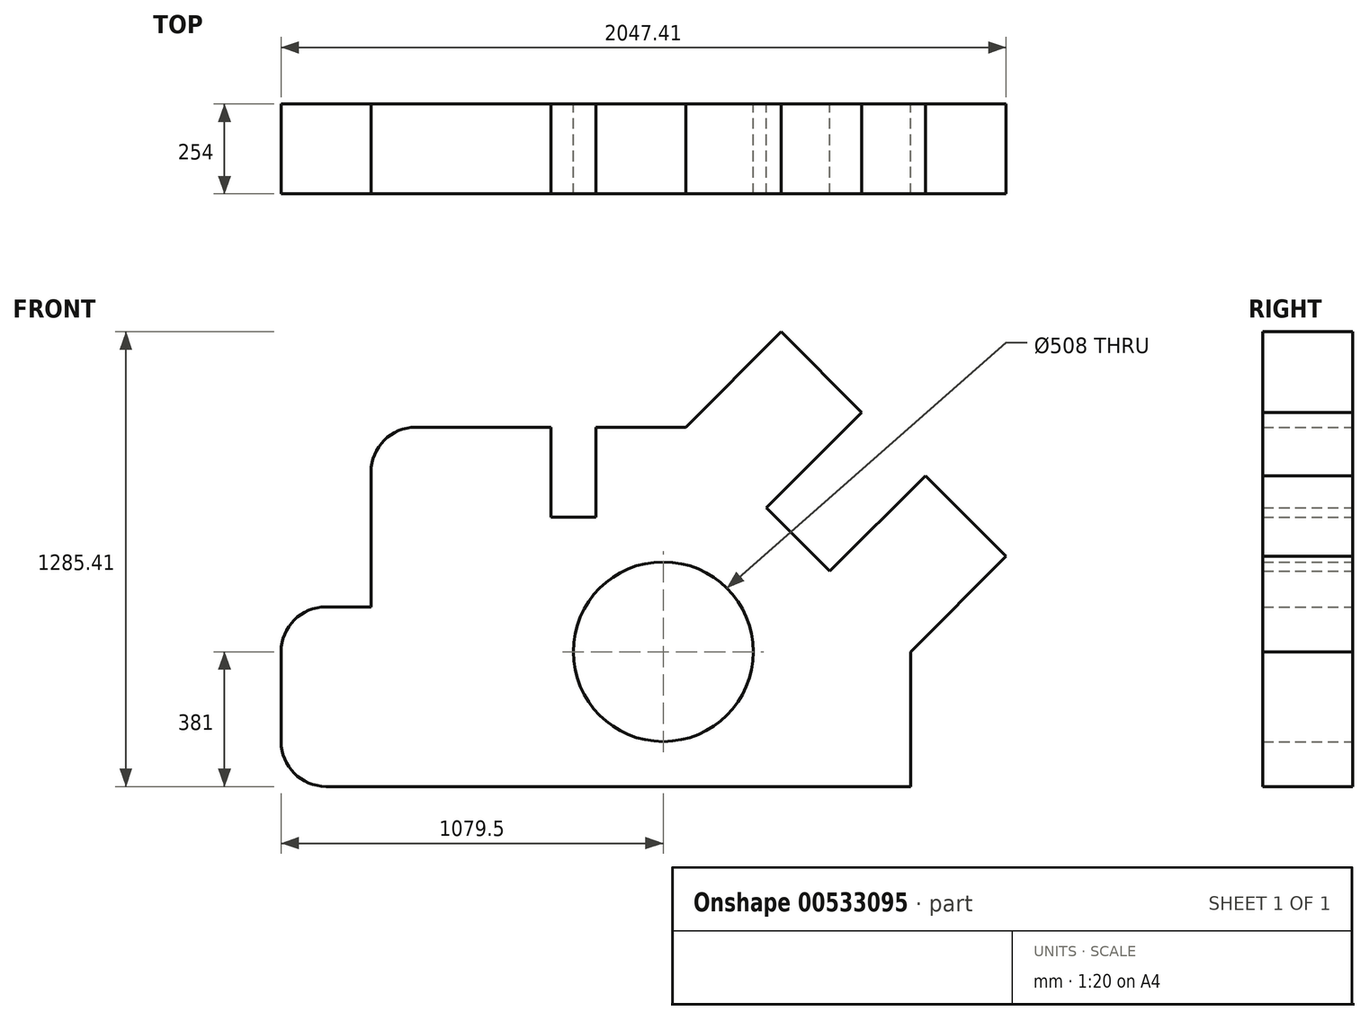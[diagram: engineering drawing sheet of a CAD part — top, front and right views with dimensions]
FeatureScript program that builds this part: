
annotation { "Feature Type Name" : "Feature", "Feature Type Description" : "" }
export const myFeature = defineFeature(function(context is Context, id is Id, definition is map)
    precondition{}
    {
        {
            var Q0;
            Q0=qCreatedBy(makeId("Front.planeOp"),FACE);
            var sketch = newSketch(context, id + "F0", { "sketchPlane" : qUnion([Q0])});
            skLineSegment(sketch, "E0", {"start": v(127, 0) * mm, "end": v(1778, 0) * mm});
            skLineSegment(sketch, "E1", {"start": v(1778, 0) * mm, "end": v(1778, 381) * mm});
            skLineSegment(sketch, "E2", {"start": v(0, 127) * mm, "end": v(0, 381) * mm});
            skCircle(sketch, "E3", {"center": v(1079.5, 381) * mm, "radius": 254 * mm});
            skLineSegment(sketch, "E4", {"start": v(127, 508) * mm, "end": v(254, 508) * mm});
            skLineSegment(sketch, "E5", {"start": v(254, 508) * mm, "end": v(254, 889) * mm});
            skLineSegment(sketch, "E6", {"start": v(381, 1016) * mm, "end": v(762, 1016) * mm});
            skLineSegment(sketch, "E7", {"start": v(762, 1016) * mm, "end": v(762, 762) * mm});
            skLineSegment(sketch, "E8", {"start": v(762, 762) * mm, "end": v(889, 762) * mm});
            skLineSegment(sketch, "E9", {"start": v(889, 762) * mm, "end": v(889, 1016) * mm});
            skLineSegment(sketch, "E10", {"start": v(889, 1016) * mm, "end": v(1143, 1016) * mm});
            skLineSegment(sketch, "E11", {"start": v(1778, 381) * mm, "end": v(2047.4, 650.4) * mm});
            skLineSegment(sketch, "E12", {"start": v(2047.4, 650.4) * mm, "end": v(1819.71, 878.1) * mm});
            skLineSegment(sketch, "E13", {"start": v(1819.71, 878.1) * mm, "end": v(1550.3, 608.7) * mm});
            skLineSegment(sketch, "E14", {"start": v(1550.3, 608.7) * mm, "end": v(1370.7, 788.3) * mm});
            skLineSegment(sketch, "E15", {"start": v(1370.7, 788.3) * mm, "end": v(1640.1, 1057.71) * mm});
            skLineSegment(sketch, "E16", {"start": v(1640.1, 1057.71) * mm, "end": v(1412.4, 1285.4) * mm});
            skLineSegment(sketch, "E17", {"start": v(1412.4, 1285.4) * mm, "end": v(1143, 1016) * mm});
            skPoint(sketch, "E18.visualSharp", {"position": v(254, 1016) * mm});
            skArc(sketch, "E18.filletArc", {"start": v(381, 1016) * mm, "mid": v(291.2, 978.8) * mm, "end": v(254, 889) * mm});
            skPoint(sketch, "E19.visualSharp", {"position": v(0, 508) * mm});
            skArc(sketch, "E19.filletArc", {"start": v(127, 508) * mm, "mid": v(37.2, 470.8) * mm, "end": v(0, 381) * mm});
            skPoint(sketch, "E20.visualSharp", {"position": v(0, 0) * mm});
            skArc(sketch, "E20.filletArc", {"start": v(0, 127) * mm, "mid": v(37.2, 37.2) * mm, "end": v(127, 0) * mm});
            skSolve(sketch);
        }
        {
            var Q0;
            Q0=makeQuery(id+"F0.imprint","IMPRINT",FACE,{"disambiguationData":[TD([[makeQuery(id+"F0.imprint","IMPRINT",EDGE,{"derivedFrom":sQuery(id+"F0.wireOp",EDGE,"E0")}),1.0]])]});
            extrude(context, id + "F1", {"entities" : qUnion([Q0]), "depth" : 254 * mm, "offsetDistance" : 25.4 * mm});
        }
    });
